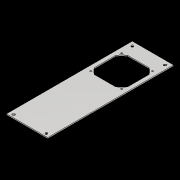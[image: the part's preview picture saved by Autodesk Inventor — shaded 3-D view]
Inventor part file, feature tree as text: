
AUTODESK INVENTOR PART (.ipt)
format: ipt  version: 2018.2 (Build 222227000, 227)  size: 188,928 bytes
history: native  units: mm
features: extrude x3, sketch x3, other x1
ambient origin geometry x8: Origin, YZ Plane, XZ Plane, XY Plane, X Axis, Y Axis, Z Axis, Center Point
bodies: Body1 (feature_tree)
feature tree (7):
  other  "ソリッド1"
  extrude  "押し出し1"  Depth=110.0mm
  extrude  "押し出し2"  Depth=340.0mm
  extrude  "押し出し3"  TaperAngle=135.0deg  [1 undecoded]
  sketch  "スケッチ1"
  sketch  "スケッチ2"
  sketch  "スケッチ3"
note: 1 required parameter value undecoded (feature->parameter linkage not recoverable at this tier; creation-order binding heuristic only, values carry confidence <= 0.55)
